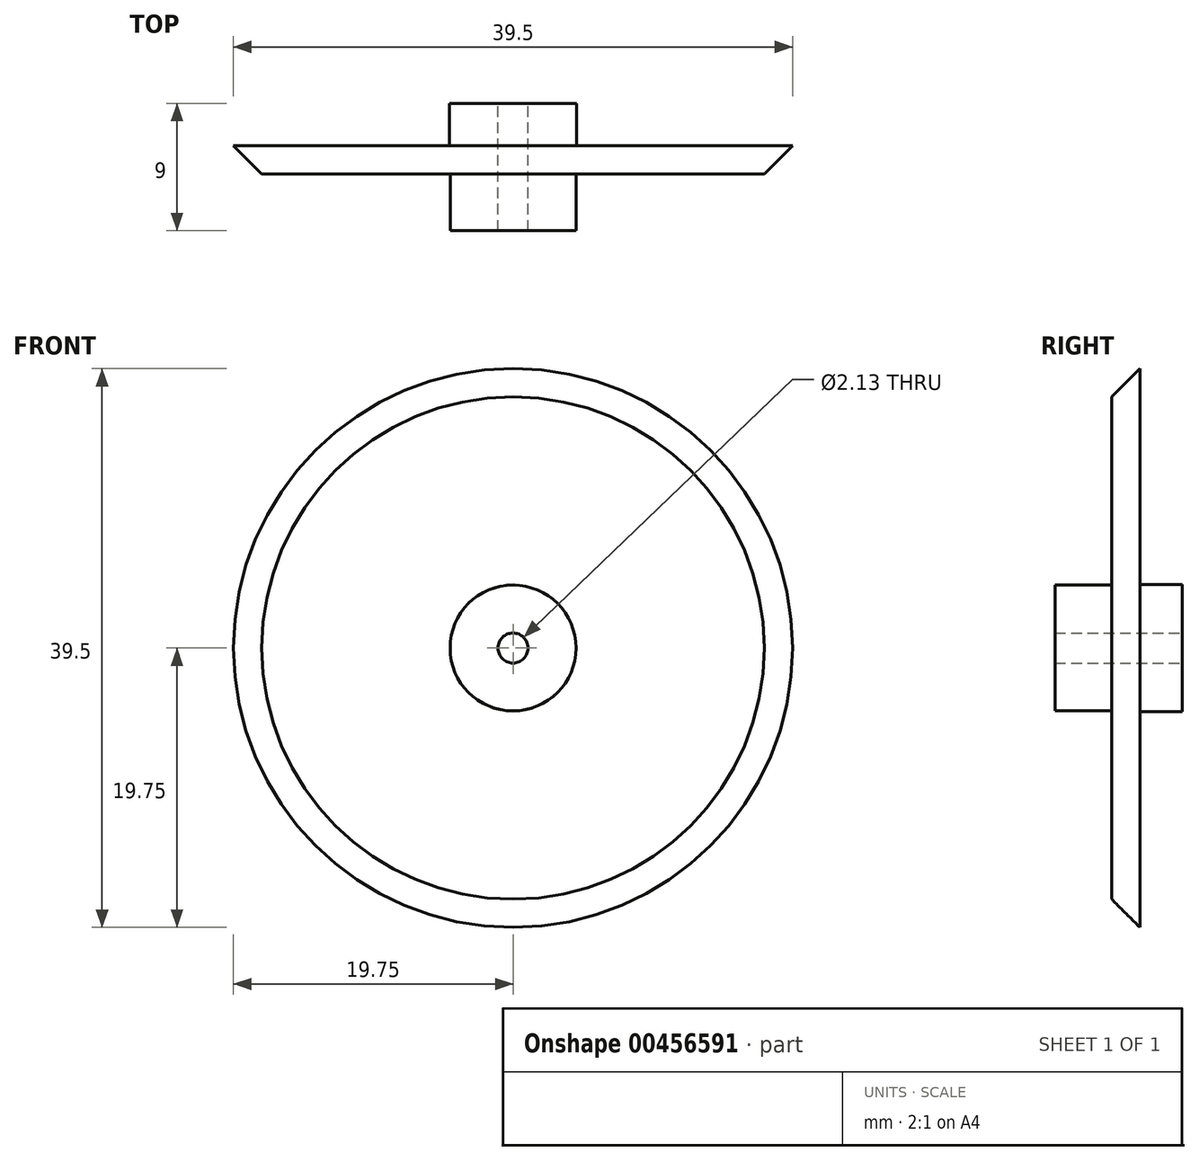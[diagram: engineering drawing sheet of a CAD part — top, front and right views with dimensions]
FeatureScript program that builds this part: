
annotation { "Feature Type Name" : "Feature", "Feature Type Description" : "" }
export const myFeature = defineFeature(function(context is Context, id is Id, definition is map)
    precondition{}
    {
        {
            var Q0;
            Q0=qCreatedBy(makeId("Front.planeOp"),FACE);
            var sketch = newSketch(context, id + "F0", { "sketchPlane" : qUnion([Q0])});
            skCircle(sketch, "E0", {"center": v(0, 0) * mm, "radius": 22.75 * mm});
            skSolve(sketch);
        }
        {
            var Q0;
            Q0 = qSketchRegion(id + "F0", true);
            extrude(context, id + "F1", {"entities" : qUnion([Q0]), "depth" : 2 * mm});
        }
        {
            var Q0;
            Q0=qCreatedBy(makeId("Front.planeOp"),FACE);
            var sketch = newSketch(context, id + "F2", { "sketchPlane" : qUnion([Q0])});
            skCircle(sketch, "E1", {"center": v(0, 0) * mm, "radius": 4.45 * mm});
            skSolve(sketch);
        }
        {
            var Q0;
            Q0 = qSketchRegion(id + "F2", true);
            extrude(context, id + "F3", {"entities" : qUnion([Q0]), "operationType" : NewBodyOperationType.ADD, "depth" : 6 * mm});
        }
        {
            var Q0;
            Q0=qCreatedBy(makeId("Front.planeOp"),FACE);
            var sketch = newSketch(context, id + "F4", { "sketchPlane" : qUnion([Q0])});
            skCircle(sketch, "E2", {"center": v(0, 0) * mm, "radius": 4.5 * mm});
            skSolve(sketch);
        }
        {
            var Q0;
            Q0 = qSketchRegion(id + "F4", true);
            extrude(context, id + "F5", {"entities" : qUnion([Q0]), "operationType" : NewBodyOperationType.ADD, "oppositeDirection" : true, "depth" : 3 * mm});
        }
        {
            var Q0;
            Q0=qCreatedBy(makeId("Front.planeOp"),FACE);
            var sketch = newSketch(context, id + "F6", { "sketchPlane" : qUnion([Q0])});
            skCircle(sketch, "E3", {"center": v(0, 0) * mm, "radius": 1.06 * mm});
            skSolve(sketch);
        }
        {
            var Q0;
            Q0 = qSketchRegion(id + "F6", true);
            extrude(context, id + "F7", {"entities" : qUnion([Q0]), "operationType" : NewBodyOperationType.REMOVE, "depth" : 6 * mm});
        }
        {
            var Q0;
            Q0=qCreatedBy(makeId("Front.planeOp"),FACE);
            var sketch = newSketch(context, id + "F8", { "sketchPlane" : qUnion([Q0])});
            skCircle(sketch, "E4", {"center": v(0, 0) * mm, "radius": 1.06 * mm});
            skSolve(sketch);
        }
        {
            var Q0;
            Q0 = qSketchRegion(id + "F8", true);
            extrude(context, id + "F9", {"entities" : qUnion([Q0]), "operationType" : NewBodyOperationType.REMOVE, "oppositeDirection" : true, "depth" : 6 * mm});
        }
        {
            var Q0;
            Q0=makeQuery(id+"F1.opExtrude","CAP_EDGE",EDGE,{"disambiguationData":[OSD([sQuery(id+"F0.wireOp",EDGE,"E0")])],"isStart":false});
            chamfer(context, id + "F10", {"entities" : qUnion([Q0]), "width" : 5 * mm, "tangentPropagation" : true});
        }
    });
